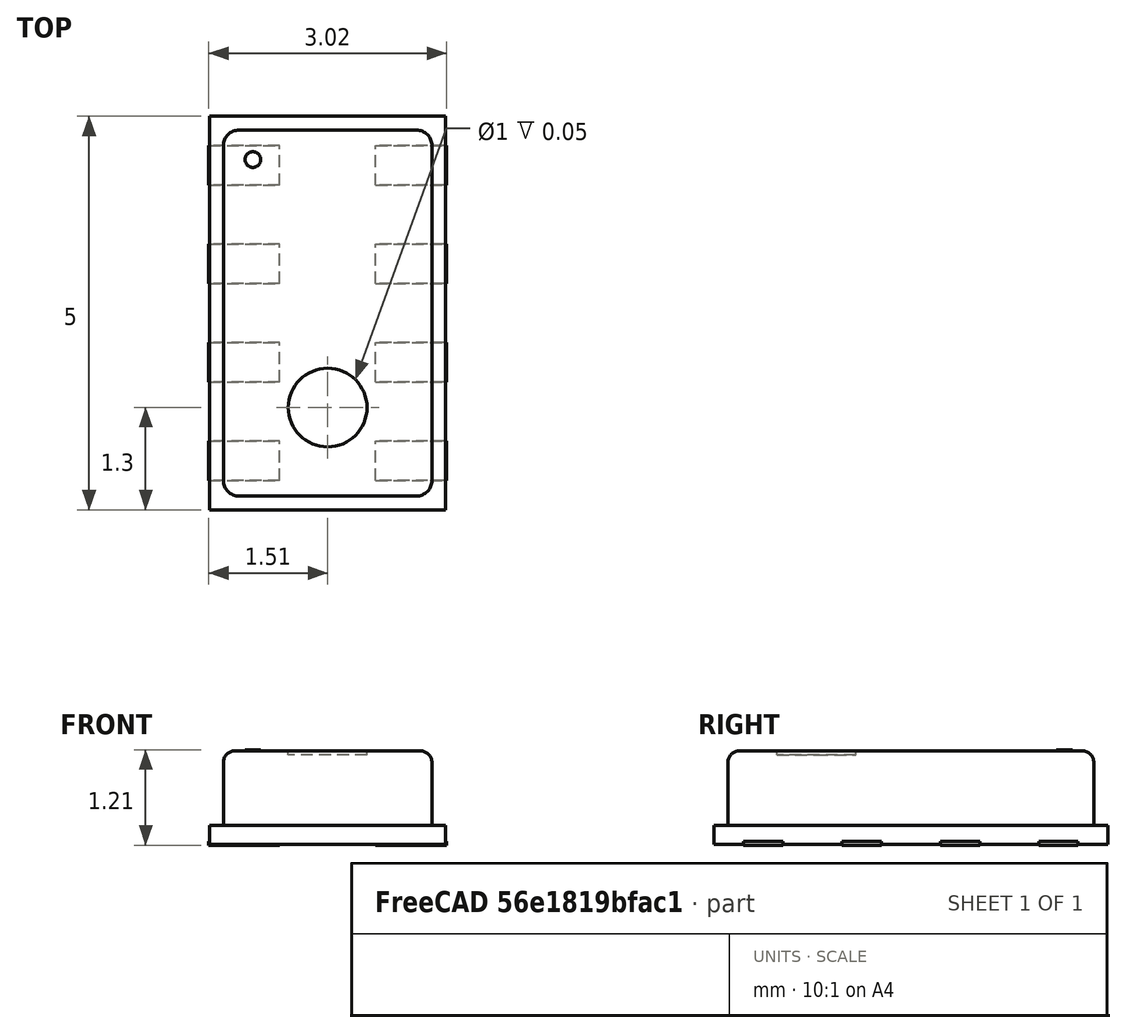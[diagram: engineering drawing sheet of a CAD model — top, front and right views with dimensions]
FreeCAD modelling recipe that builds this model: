
FCSTD DOCUMENT  (FreeCAD 0.17R10887 (Git))
Label: MPL115A1
License: All rights reserved
LicenseURL: http://en.wikipedia.org/wiki/All_rights_reserved
objects: Part::Box×11, Part::MultiFuse×4, Part::Cylinder×3, Part::Fillet×2, Part::Cut×1, Part::Fuse×1
note: 22 computed .brp shape members not serialized (recipe doc carries the construction recipe); baked Part::Feature solids carry a one-line shape summary decoded from their .brp

FEATURE [Part::Box] Box  label="Base"
  AttacherType = Attacher::AttachEngine3D
  Height = 0.14
  Length = 3
  Placement = pos=(-1.5,-2.5,0.01) rot=(0,0,1;0rad)
  Width = 5
FEATURE [Part::Box] Box001  label="Flange"
  AttacherType = Attacher::AttachEngine3D
  Height = 0.1
  Length = 3
  Placement = pos=(-1.5,-2.5,0.15) rot=(0,0,1;0rad)
  Width = 5
FEATURE [Part::Box] Box002  label="Cube"
  AttacherType = Attacher::AttachEngine3D
  Height = 0.95
  Length = 2.65
  Placement = pos=(-1.325,-2.325,0.25) rot=(0,0,1;0rad)
  Width = 4.65
  expr: Placement.Base.y = -4.6500000000000004 / 2
  expr: Placement.Base.x = -2.6499999999999999 / 2
FEATURE [Part::Fillet] Fillet
  Base = -> Box002
  Edges = 4 edges r=0.2: [Edge1,Edge3,Edge5,Edge7]
FEATURE [Part::Fillet] Fillet001
  Base = -> Fillet
  Edges = 8 edges r=0.15: [Edge1,Edge5,Edge6,Edge7,Edge8,Edge9,Edge10,Edge11]
FEATURE [Part::Cylinder] Cylinder
  Angle = 360
  AttacherType = Attacher::AttachEngine3D
  Height = 0.2
  Placement = pos=(0,-1.2,1.1) rot=(0,0,1;0rad)
  Radius = 0.5
FEATURE [Part::Cut] Cut
  Base = -> Fillet001
  Tool = -> Cylinder
FEATURE [Part::Cylinder] Cylinder001  label="Air vent hole"
  Angle = 360
  AttacherType = Attacher::AttachEngine3D
  Height = 0.1
  Placement = pos=(0,-1.2,1.05) rot=(0,0,1;0rad)
  Radius = 1
FEATURE [Part::Fuse] Fusion  label="Body"
  Base = -> Box001
  Tool = -> Cut
FEATURE [Part::Box] Box003  label="Cube001"
  AttacherType = Attacher::AttachEngine3D
  Height = 0.05
  Length = 0.9
  Placement = pos=(0.61,0.375,0) rot=(0,0,1;0rad)
  Width = 0.5
  expr: Placement.Base.y = 0.625 - 0.25
  expr: Placement.Base.x = 1.05 - 0.45000000000000001 + 0.01
FEATURE [Part::Box] Box004  label="Cube002"
  AttacherType = Attacher::AttachEngine3D
  Height = 0.05
  Length = 0.9
  Placement = pos=(0.61,1.625,0) rot=(0,0,1;0rad)
  Width = 0.5
  expr: Placement.Base.y = 0.625 + 1.25 - 0.25
  expr: Placement.Base.x = 1.05 - 0.45000000000000001 + 0.01
FEATURE [Part::Box] Box005  label="Cube003"
  AttacherType = Attacher::AttachEngine3D
  Height = 0.05
  Length = 0.9
  Placement = pos=(0.61,-0.875,0) rot=(0,0,1;0rad)
  Width = 0.5
  expr: Placement.Base.y = -0.625 - 0.25
  expr: Placement.Base.x = 1.05 - 0.45000000000000001 + 0.01
FEATURE [Part::Box] Box006  label="Cube004"
  AttacherType = Attacher::AttachEngine3D
  Height = 0.05
  Length = 0.9
  Placement = pos=(0.61,-2.125,0) rot=(0,0,1;0rad)
  Width = 0.5
  expr: Placement.Base.y = -0.625 - 1.25 - 0.25
  expr: Placement.Base.x = 1.05 - 0.45000000000000001 + 0.01
FEATURE [Part::MultiFuse] Fusion001
  Shapes = -> [Box005,Box003,Box006,Box004]
FEATURE [Part::Box] Box007  label="Cube005"
  AttacherType = Attacher::AttachEngine3D
  Height = 0.05
  Length = 0.9
  Placement = pos=(0.61,-0.875,0) rot=(0,0,1;0rad)
  Width = 0.5
  expr: Placement.Base.y = -0.625 - 0.25
  expr: Placement.Base.x = 1.05 - 0.45000000000000001 + 0.01
FEATURE [Part::Box] Box008  label="Cube006"
  AttacherType = Attacher::AttachEngine3D
  Height = 0.05
  Length = 0.9
  Placement = pos=(0.61,0.375,0) rot=(0,0,1;0rad)
  Width = 0.5
  expr: Placement.Base.y = 0.625 - 0.25
  expr: Placement.Base.x = 1.05 - 0.45000000000000001 + 0.01
FEATURE [Part::Box] Box009  label="Cube007"
  AttacherType = Attacher::AttachEngine3D
  Height = 0.05
  Length = 0.9
  Placement = pos=(0.61,-2.125,0) rot=(0,0,1;0rad)
  Width = 0.5
  expr: Placement.Base.y = -0.625 - 1.25 - 0.25
  expr: Placement.Base.x = 1.05 - 0.45000000000000001 + 0.01
FEATURE [Part::Box] Box010  label="Cube008"
  AttacherType = Attacher::AttachEngine3D
  Height = 0.05
  Length = 0.9
  Placement = pos=(0.61,1.625,0) rot=(0,0,1;0rad)
  Width = 0.5
  expr: Placement.Base.y = 0.625 + 1.25 - 0.25
  expr: Placement.Base.x = 1.05 - 0.45000000000000001 + 0.01
FEATURE [Part::MultiFuse] Fusion002
  Placement = pos=(-2.12,0,0) rot=(0,0,1;0rad)
  Shapes = -> [Box007,Box008,Box009,Box010]
FEATURE [Part::MultiFuse] Fusion003  label="Pads"
  Shapes = -> [Fusion001,Fusion002]
FEATURE [Part::Cylinder] Cylinder002  label="Pin 1 marker"
  Angle = 360
  AttacherType = Attacher::AttachEngine3D
  Height = 0.21
  Placement = pos=(-0.95,1.95,1) rot=(0,0,1;0rad)
  Radius = 0.1
FEATURE [Part::MultiFuse] Fusion004  label="MPL115A1"
  Shapes = -> [Box,Fusion003,Fusion,Cylinder001,Cylinder002]
